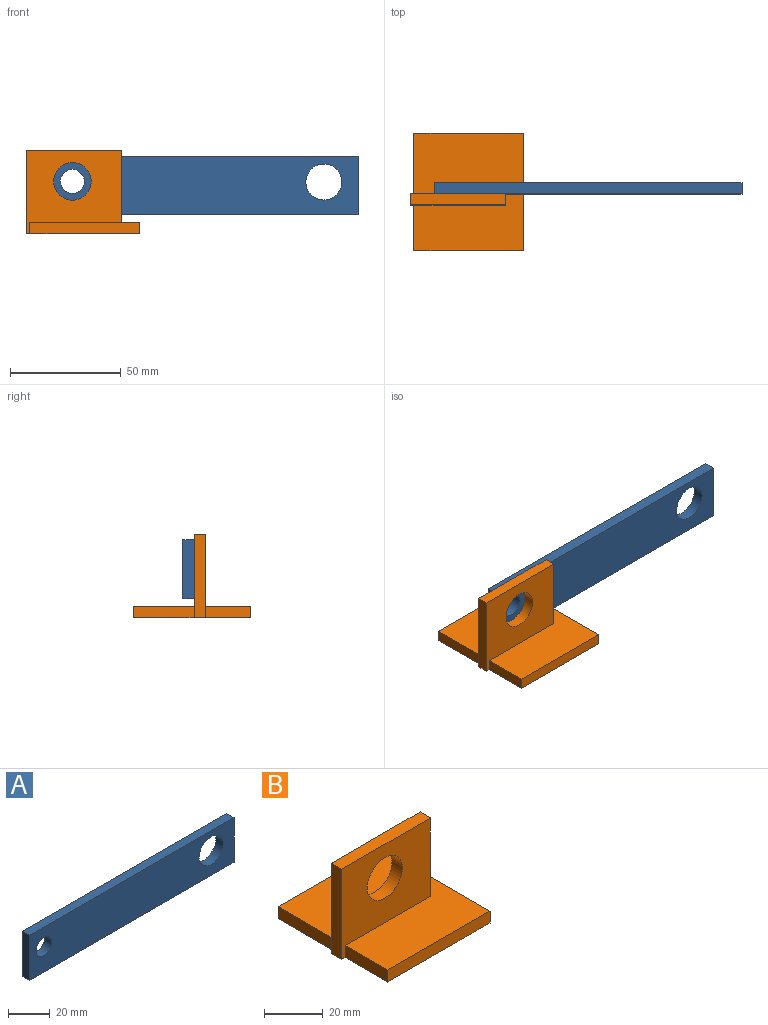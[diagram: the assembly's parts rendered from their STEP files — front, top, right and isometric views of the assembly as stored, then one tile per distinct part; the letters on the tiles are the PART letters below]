
ASSEMBLY  parts=2 mates=1
PART A: 8 faces, bbox 138.9x5x26.5 mm
  f0: plane 138.93x5mm, normal (0,0,1), area 694.6mm2, adj f1,f5,f6,f7
  f1: plane 26.46x5mm, normal (-1,0,0), area 132.3mm2, adj f0,f2,f6,f7
  f2: plane 138.93x5mm, normal (0,0,-1), area 694.6mm2, adj f1,f5,f6,f7
  f3: cylinder r=5.41mm len=10.83mm, axis (0,1,0), area 170mm2, adj f6,f7
  f4: cylinder r=8.12mm len=16.24mm, axis (0,1,0), area 255.1mm2, adj f6,f7
  f5: plane 26.24x5mm, normal (1,0,0), area 131.2mm2, adj f0,f2,f6,f7
  f6: plane 138.93x26.46mm, normal (0,-1,0), area 3361.7mm2, adj f0,f1,f2,f3,f4,f5
  f7: plane 138.93x26.46mm, normal (0,1,0), area 3361.7mm2, adj f0,f1,f2,f3,f4,f5
PART B: 13 faces, bbox 51.2x53.1x37.8 mm
  f0: plane 27.47x5mm, normal (-1,0,0), area 137.3mm2, adj f1,f5,f6,f8
  f1: plane 49.39x5mm, normal (0,1,0), area 246.9mm2, adj f0,f4,f5,f6
  f2: plane 20.61x5mm, normal (-1,0,0), area 103mm2, adj f3,f5,f6,f7
  f3: plane 49.39x5mm, normal (0,-1,0), area 246.9mm2, adj f2,f4,f5,f6
  f4: plane 53.08x5mm, normal (1,0,0), area 265.4mm2, adj f1,f3,f5,f6
  f5: plane 53.08x49.39mm, normal (0,0,1), area 2415.4mm2, adj f0,f1,f2,f3,f4,f7,f8,f10
  f6: plane 53.08x51.17mm, normal (0,0,-1), area 2630.4mm2, adj f0,f1,f2,f3,f4,f7,f8,f9
  f7: plane 43x37.76mm, normal (0,-1,0), area 1192mm2, adj f2,f5,f6,f9,f10,f11,f12
  f8: plane 43x37.76mm, normal (0,1,0), area 1192mm2, adj f0,f5,f6,f9,f10,f11,f12
  f9: plane 37.76x5mm, normal (-1,0,0), area 188.8mm2, adj f6,f7,f8,f11
  f10: plane 32.76x5mm, normal (1,0,0), area 163.8mm2, adj f5,f7,f8,f11
  f11: plane 43x5mm, normal (0,0,1), area 215mm2, adj f7,f8,f9,f10
  f12: cylinder r=8.48mm len=16.95mm, axis (0,1,0), area 266.3mm2, adj f7,f8
PLACE A t=(-26.34,-63.82,-17.14)mm
PLACE B t=(-121.17,-68.82,-11.44)mm fixed
MATE revolute A.f3 <-> B.f12  axis (0,-1,0) through (-130.82,-68.82,12.24)mm
